# Revit family: spectral_stora_stora-lk-i-led_d1900_840_os-da_b736
name_source: partatom
category: Lighting Fixtures
revit_build: Autodesk Revit 2016 (Build: 20150220_1215(x64)
units: mm (PartAtom-declared; Revit-internal decimal feet)

## family parameters
Cut with Voids When Loaded = No
Host = Face
Light Source = No
Part Type = Normal
Room Calculation Point = No
Round Connector Dimension = Use Diameter
Shared = No

## types (1)
- SPECTRAL STORA (1 x )
    Apparent Load = 0 VA
    CIE Flux Codes = 47 78 95 63 77
    Control Gear = Electronic transformer
    Default Elevation = 1800 mm
    Description = SPC0630019
STORA LED chandelier

Design:
Ring-shaped luminaire element with opal acrylic glass panels mounted in a ring profile frame made of power-coated aluminium. LED linear modules are
evenly mounted on a metal base in the ring profile frame. Additional LED linear modules arranged facing upwards for the indirect lighting component. The top of the luminaire is covered by clear PMMA panels. The luminaire is suspended by six trapezoidal wire pendants with ceiling fixture and transparent connecting cable with round ceiling junction box. The cable length can be adjusted at the ceiling junction box, the steel wire can be steplessly height adjusted. The steel body of the ceiling junction box houses the electrical components and electronic ballast. Electrical connection by means of connector block with cable strain relief. Mechanical ceiling fixture by means of an oblong hole screw connection to a round powder-coated mounting box. The luminaire is configured with heat-resistant wiring. Homogeneous illumination of the light surface. Also in a dimmable version. Light colours 4000 K (840) and 3000K (830). Protection rating IP20, safety class I.

Colour:
Housing – similar to RAL 9016 white silk matt;
Frame – similar to RAL 9016 white silk matt
    Height = 100 mm  [stored 0.328084 ft]
    Lamp = 1 x
    Lamp count = 1
    Length = 1900 mm
    Luminous efficacy = 0 lm/W
    Manufacturer = Ridi
    ModVariant = No
    Model = STORA-LK-I-LED D1900/840 OS-DA
    Mounting Place = Ceiling
    Mounting Type = Pendant
    Number of Poles = 1
    OnlyDefault = Yes
    Power Factor = 1
    Product Name = SPECTRAL STORA
    Product group = Pendant luminaire
    ProductGroupID = 9
    Protection Class = Protection class
    Protection Degree = Degree of protection
    RlxData = <blob elided: 16637 chars, md5=c0e1d560>
    Socket = socket
    Standby Power = 0 W
    System Light Flux = 0 lm
    System Power = 0 W
    Type Image = stora-lk.jpg
    URL = http://reluxnet.relux.com
    VarID = 1
    Voltage = 0 V
    Weight = 0.00 kg
    Width = 0 mm  [stored 0 ft]

note: [stored X ft] marks values corroborated as IEEE doubles in the binary element streams (Revit-internal decimal feet)

## geometry (parser evidence)
native form markers: Blend x4, Sweep x14
no freeform markers — native parametric forms only
